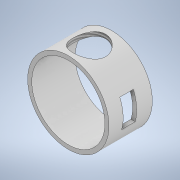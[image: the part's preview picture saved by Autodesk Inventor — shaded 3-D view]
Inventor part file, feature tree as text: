
AUTODESK INVENTOR PART (.ipt)
format: ipt  version: 2021 (Build 250183000, 183)  size: 138,752 bytes
history: native  units: mm
features: extrude x3, sketch x3, other x1
ambient origin geometry x8: Origin, YZ Plane, XZ Plane, XY Plane, X Axis, Y Axis, Z Axis, Center Point
bodies: Solide1 (feature_tree)
feature tree (7):
  extrude  "Extrusion1"  Depth=60.0mm
  extrude  "Extrusion2"  Depth=54.0mm
  other  "Filetage1"
  extrude  "Extrusion3"  Depth=32.0mm TaperAngle=0.0deg
  sketch  "Esquisse1"
  sketch  "Esquisse2"
  sketch  "Esquisse3"
